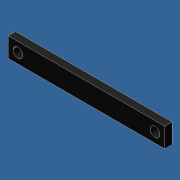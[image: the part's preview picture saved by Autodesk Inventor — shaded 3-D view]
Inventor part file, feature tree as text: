
AUTODESK INVENTOR PART (.ipt)
format: ipt  version: 2012 (Build 160160000, 160)  size: 75,776 bytes
history: native  units: in
note: dims shown in document units (in); Inventor stores cm internally (conversion verified against a paired STEP export)
features: extrude x1, sketch x1
ambient origin geometry x8: Origin, YZ Plane, XZ Plane, XY Plane, X Axis, Y Axis, Z Axis, Center Point
bodies: Solid1 (feature_tree)
feature tree (2):
  extrude  "Extrusion1"  Depth=1.0in
  sketch  "Sketch1"  dims[d0=8.0in d1=1.0in d2=0.5in d3=0.5in d4=0.5in d5=0.5in d6=0.38in d7=0.0in d9=0.5in d10=0.5in]
